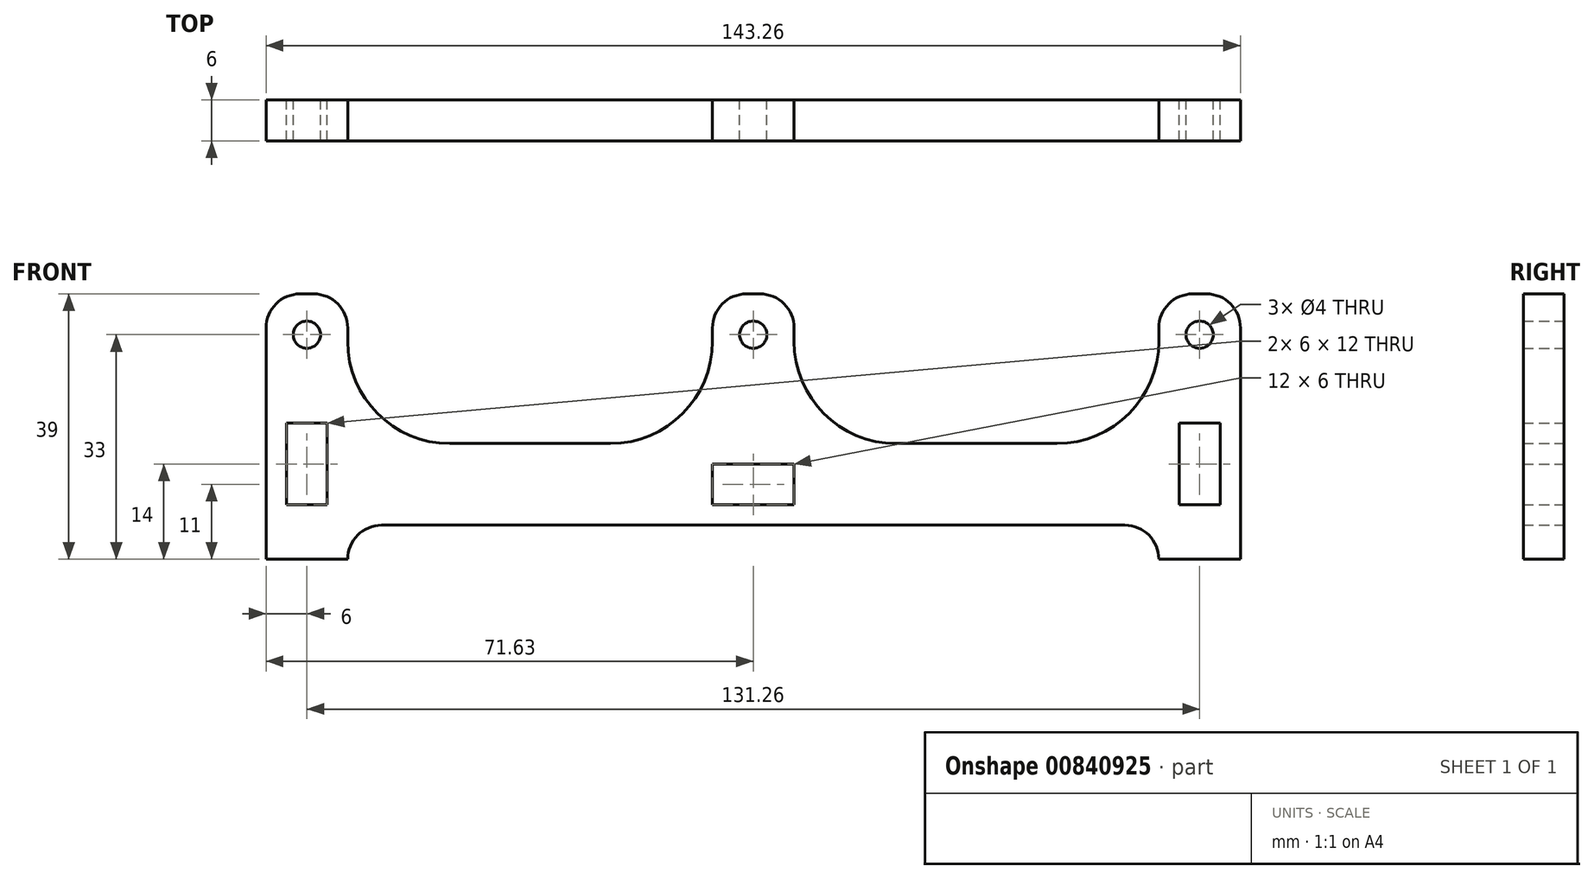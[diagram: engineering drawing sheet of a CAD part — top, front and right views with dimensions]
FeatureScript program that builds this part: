
annotation { "Feature Type Name" : "Feature", "Feature Type Description" : "" }
export const myFeature = defineFeature(function(context is Context, id is Id, definition is map)
    precondition{}
    {
        {
            var Q0;
            Q0=qCreatedBy(makeId("Front.planeOp"),FACE);
            var sketch = newSketch(context, id + "F0", { "sketchPlane" : qUnion([Q0])});
            skLineSegment(sketch, "E0", {"start": v(0, 51.62) * mm, "end": v(0, -21.63) * mm, "construction": true});
            skLineSegment(sketch, "E1", {"start": v(0, 39) * mm, "end": v(-1, 39) * mm});
            skLineSegment(sketch, "E2", {"start": v(-6, 34) * mm, "end": v(-6, 32) * mm});
            skLineSegment(sketch, "E3", {"start": v(-21, 17) * mm, "end": v(-44.63, 17) * mm});
            skLineSegment(sketch, "E4", {"start": v(-59.63, 32) * mm, "end": v(-59.63, 34) * mm});
            skLineSegment(sketch, "E5", {"start": v(-64.63, 39) * mm, "end": v(-66.63, 39) * mm});
            skLineSegment(sketch, "E6", {"start": v(-71.63, 34) * mm, "end": v(-71.63, 0) * mm});
            skLineSegment(sketch, "E7", {"start": v(-71.63, 0) * mm, "end": v(-59.63, 0) * mm});
            skLineSegment(sketch, "E8", {"start": v(-59.63, 0) * mm, "end": v(-59.63, 0) * mm});
            skLineSegment(sketch, "E9", {"start": v(-54.63, 5) * mm, "end": v(0, 5) * mm});
            skPoint(sketch, "E10.visualSharp", {"position": v(-71.63, 39) * mm});
            skArc(sketch, "E10.filletArc", {"start": v(-66.63, 39) * mm, "mid": v(-70.17, 37.54) * mm, "end": v(-71.63, 34) * mm});
            skPoint(sketch, "E11.visualSharp", {"position": v(-59.63, 5) * mm});
            skArc(sketch, "E11.filletArc", {"start": v(-54.63, 5) * mm, "mid": v(-58.17, 3.54) * mm, "end": v(-59.63, 0) * mm});
            skPoint(sketch, "E12.visualSharp", {"position": v(-59.63, 39) * mm});
            skArc(sketch, "E12.filletArc", {"start": v(-59.63, 34) * mm, "mid": v(-61.1, 37.54) * mm, "end": v(-64.63, 39) * mm});
            skPoint(sketch, "E13.visualSharp", {"position": v(-6, 39) * mm});
            skArc(sketch, "E13.filletArc", {"start": v(-1, 39) * mm, "mid": v(-4.54, 37.54) * mm, "end": v(-6, 34) * mm});
            skPoint(sketch, "E14.visualSharp", {"position": v(-59.63, 17) * mm});
            skArc(sketch, "E14.filletArc", {"start": v(-59.63, 32) * mm, "mid": v(-55.24, 21.4) * mm, "end": v(-44.63, 17) * mm});
            skPoint(sketch, "E15.visualSharp", {"position": v(-6, 17) * mm});
            skArc(sketch, "E15.filletArc", {"start": v(-21, 17) * mm, "mid": v(-10.4, 21.4) * mm, "end": v(-6, 32) * mm});
            skCircle(sketch, "E16", {"center": v(-65.63, 33) * mm, "radius": 2 * mm});
            skArc(sketch, "E17.1.0.0", {"start": v(0, 35) * mm, "mid": v(-2, 33) * mm, "end": v(0, 31) * mm});
            skLineSegment(sketch, "E17.direction1", {"start": v(-65.63, 33) * mm, "end": v(0, 33) * mm, "construction": true});
            skLineSegment(sketch, "E18.bottom", {"start": v(-68.63, 20) * mm, "end": v(-62.63, 20) * mm});
            skLineSegment(sketch, "E18.top", {"start": v(-68.63, 8) * mm, "end": v(-62.63, 8) * mm});
            skLineSegment(sketch, "E18.left", {"start": v(-68.63, 20) * mm, "end": v(-68.63, 8) * mm});
            skLineSegment(sketch, "E18.right", {"start": v(-62.63, 20) * mm, "end": v(-62.63, 8) * mm});
            skLineSegment(sketch, "E19.bottom", {"start": v(0, 14) * mm, "end": v(-6, 14) * mm});
            skLineSegment(sketch, "E19.top", {"start": v(0, 8) * mm, "end": v(-6, 8) * mm});
            skLineSegment(sketch, "E19.left", {"start": v(0, 14) * mm, "end": v(0, 8) * mm});
            skLineSegment(sketch, "E19.right", {"start": v(-6, 14) * mm, "end": v(-6, 8) * mm});
            skLineSegment(sketch, "E20.MirrorCS", {"start": v(59.63, 32) * mm, "end": v(59.63, 34) * mm});
            skLineSegment(sketch, "E21.MirrorCS", {"start": v(64.63, 39) * mm, "end": v(66.63, 39) * mm});
            skLineSegment(sketch, "E22.MirrorCS", {"start": v(6, 34) * mm, "end": v(6, 32) * mm});
            skLineSegment(sketch, "E23.MirrorCS", {"start": v(0, 39) * mm, "end": v(1, 39) * mm});
            skArc(sketch, "E24.MirrorCS", {"start": v(0, 35) * mm, "mid": v(2, 33) * mm, "end": v(0, 31) * mm});
            skLineSegment(sketch, "E25.MirrorCS", {"start": v(0, 14) * mm, "end": v(6, 14) * mm});
            skArc(sketch, "E26.MirrorCS", {"start": v(59.63, 32) * mm, "mid": v(55.24, 21.4) * mm, "end": v(44.63, 17) * mm});
            skLineSegment(sketch, "E27.MirrorCS", {"start": v(71.63, 0) * mm, "end": v(59.63, 0) * mm});
            skCircle(sketch, "E28.MirrorC", {"center": v(65.63, 33) * mm, "radius": 2 * mm});
            skLineSegment(sketch, "E29.MirrorCS", {"start": v(65.63, 33) * mm, "end": v(0, 33) * mm, "construction": true});
            skPoint(sketch, "E30.MirrorP", {"position": v(6, 17) * mm});
            skLineSegment(sketch, "E31.MirrorCS", {"start": v(6, 14) * mm, "end": v(6, 8) * mm});
            skLineSegment(sketch, "E32.MirrorCS", {"start": v(68.63, 20) * mm, "end": v(62.63, 20) * mm});
            skLineSegment(sketch, "E33.MirrorCS", {"start": v(71.63, 34) * mm, "end": v(71.63, 0) * mm});
            skLineSegment(sketch, "E34.MirrorCS", {"start": v(68.63, 20) * mm, "end": v(68.63, 8) * mm});
            skLineSegment(sketch, "E35.MirrorCS", {"start": v(0, 8) * mm, "end": v(6, 8) * mm});
            skPoint(sketch, "E36.MirrorP", {"position": v(59.63, 39) * mm});
            skLineSegment(sketch, "E37.MirrorCS", {"start": v(68.63, 8) * mm, "end": v(62.63, 8) * mm});
            skArc(sketch, "E38.MirrorCS", {"start": v(54.63, 5) * mm, "mid": v(58.17, 3.54) * mm, "end": v(59.63, 0) * mm});
            skLineSegment(sketch, "E39.MirrorCS", {"start": v(54.63, 5) * mm, "end": v(0, 5) * mm});
            skLineSegment(sketch, "E40.MirrorCS", {"start": v(62.63, 20) * mm, "end": v(62.63, 8) * mm});
            skPoint(sketch, "E41.MirrorP", {"position": v(59.63, 5) * mm});
            skPoint(sketch, "E42.MirrorP", {"position": v(6, 39) * mm});
            skPoint(sketch, "E43.MirrorP", {"position": v(71.63, 39) * mm});
            skLineSegment(sketch, "E44.MirrorCS", {"start": v(59.63, 0) * mm, "end": v(59.63, 0) * mm});
            skArc(sketch, "E45.MirrorCS", {"start": v(21, 17) * mm, "mid": v(10.4, 21.4) * mm, "end": v(6, 32) * mm});
            skArc(sketch, "E46.MirrorCS", {"start": v(66.63, 39) * mm, "mid": v(70.17, 37.54) * mm, "end": v(71.63, 34) * mm});
            skLineSegment(sketch, "E47.MirrorCS", {"start": v(21, 17) * mm, "end": v(44.63, 17) * mm});
            skArc(sketch, "E48.MirrorCS", {"start": v(59.63, 34) * mm, "mid": v(61.1, 37.54) * mm, "end": v(64.63, 39) * mm});
            skArc(sketch, "E49.MirrorCS", {"start": v(1, 39) * mm, "mid": v(4.54, 37.54) * mm, "end": v(6, 34) * mm});
            skPoint(sketch, "E50.MirrorP", {"position": v(59.63, 17) * mm});
            skSolve(sketch);
        }
        {
            var Q0;
            Q0 = qSketchRegion(id + "F0", true);
            extrude(context, id + "F1", {"entities" : qUnion([Q0]), "depth" : 6 * mm, "offsetDistance" : 25 * mm});
        }
    });
